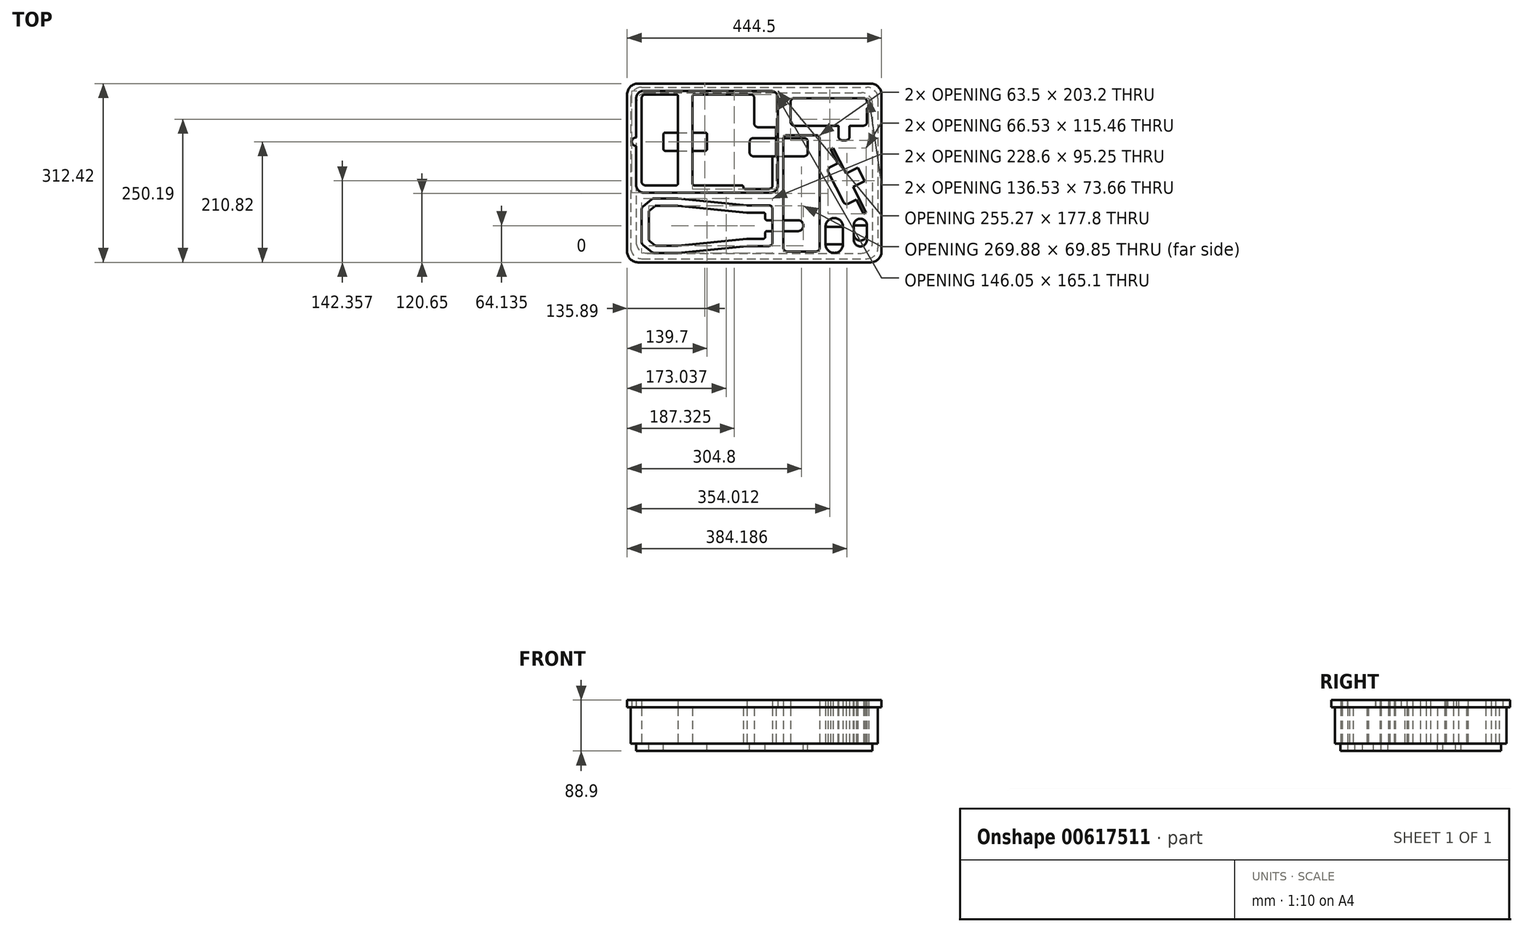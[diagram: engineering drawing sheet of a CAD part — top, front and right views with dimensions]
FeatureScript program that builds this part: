
annotation { "Feature Type Name" : "Feature", "Feature Type Description" : "" }
export const myFeature = defineFeature(function(context is Context, id is Id, definition is map)
    precondition{}
    {
        {
            var Q0;
            Q0=qCreatedBy(makeId("Top.planeOp"),FACE);
            var sketch = newSketch(context, id + "F0", { "sketchPlane" : qUnion([Q0])});
            skLineSegment(sketch, "E0.bottom", {"start": v(-196.85, 149.86) * mm, "end": v(196.85, 149.86) * mm});
            skLineSegment(sketch, "E0.top", {"start": v(-196.85, -149.86) * mm, "end": v(196.85, -149.86) * mm});
            skLineSegment(sketch, "E0.left", {"start": v(-215.9, 130.81) * mm, "end": v(-215.9, -130.81) * mm});
            skLineSegment(sketch, "E0.right", {"start": v(215.9, 130.81) * mm, "end": v(215.9, -130.8) * mm});
            skLineSegment(sketch, "E1.bottom", {"start": v(-196.85, -15.24) * mm, "end": v(-196.85, 130.81) * mm});
            skLineSegment(sketch, "E1.top", {"start": v(31.75, -21.59) * mm, "end": v(31.75, 26.04) * mm});
            skLineSegment(sketch, "E1.right", {"start": v(-190.5, 137.16) * mm, "end": v(-136.52, 137.16) * mm});
            skLineSegment(sketch, "E2.bottom", {"start": v(124.46, -93.98) * mm, "end": v(154.94, -93.98) * mm});
            skLineSegment(sketch, "E2.top", {"start": v(124.46, -124.46) * mm, "end": v(154.94, -124.46) * mm});
            skLineSegment(sketch, "E2.left", {"start": v(124.46, -93.98) * mm, "end": v(124.46, -124.46) * mm});
            skLineSegment(sketch, "E2.right", {"start": v(154.94, -93.98) * mm, "end": v(154.94, -124.46) * mm});
            skLineSegment(sketch, "E3", {"start": v(142.6, -24.8) * mm, "end": v(186.74, -2.32) * mm, "construction": true});
            skLineSegment(sketch, "E4", {"start": v(142.6, -24.8) * mm, "end": v(155.87, -50.83) * mm});
            skLineSegment(sketch, "E5", {"start": v(164.4, -53.6) * mm, "end": v(177.99, -46.7) * mm});
            skLineSegment(sketch, "E6", {"start": v(177.99, -46.7) * mm, "end": v(190.67, -71.59) * mm});
            skLineSegment(sketch, "E7", {"start": v(190.67, -71.59) * mm, "end": v(195.2, -69.28) * mm});
            skLineSegment(sketch, "E8", {"start": v(160.32, -0.82) * mm, "end": v(180.68, 9.56) * mm});
            skLineSegment(sketch, "E9", {"start": v(180.68, 9.56) * mm, "end": v(186.74, -2.32) * mm});
            skPoint(sketch, "E10.visualSharp", {"position": v(158.75, -56.5) * mm});
            skArc(sketch, "E10.filletArc", {"start": v(155.87, -50.83) * mm, "mid": v(159.56, -54) * mm, "end": v(164.4, -53.6) * mm});
            skArc(sketch, "E11.MirrorCS", {"start": v(129.35, 1.22) * mm, "mid": v(128.96, 6.06) * mm, "end": v(132.12, 9.76) * mm});
            skLineSegment(sketch, "E12.MirrorCS", {"start": v(145.7, 16.68) * mm, "end": v(133.02, 41.57) * mm});
            skLineSegment(sketch, "E13.MirrorCS", {"start": v(132.12, 9.76) * mm, "end": v(145.7, 16.68) * mm});
            skPoint(sketch, "E14.MirrorP", {"position": v(126.46, 6.88) * mm});
            skLineSegment(sketch, "E15.MirrorCS", {"start": v(172.42, -24.58) * mm, "end": v(192.8, -14.2) * mm});
            skLineSegment(sketch, "E16.MirrorCS", {"start": v(142.6, -24.8) * mm, "end": v(129.35, 1.22) * mm});
            skLineSegment(sketch, "E17.MirrorCS", {"start": v(192.8, -14.2) * mm, "end": v(186.74, -2.32) * mm});
            skLineSegment(sketch, "E18", {"start": v(172.42, -24.58) * mm, "end": v(195.2, -69.28) * mm});
            skPoint(sketch, "E19.visualSharp", {"position": v(-215.9, 149.86) * mm});
            skArc(sketch, "E19.filletArc", {"start": v(-196.85, 149.86) * mm, "mid": v(-210.32, 144.28) * mm, "end": v(-215.9, 130.81) * mm});
            skPoint(sketch, "E20.visualSharp", {"position": v(215.9, 149.86) * mm});
            skArc(sketch, "E20.filletArc", {"start": v(215.9, 130.81) * mm, "mid": v(210.32, 144.28) * mm, "end": v(196.85, 149.86) * mm});
            skPoint(sketch, "E21.visualSharp", {"position": v(215.9, -149.86) * mm});
            skArc(sketch, "E21.filletArc", {"start": v(196.85, -149.86) * mm, "mid": v(210.32, -144.28) * mm, "end": v(215.9, -130.8) * mm});
            skPoint(sketch, "E22.visualSharp", {"position": v(-215.9, -149.86) * mm});
            skArc(sketch, "E22.filletArc", {"start": v(-215.9, -130.81) * mm, "mid": v(-210.32, -144.28) * mm, "end": v(-196.85, -149.86) * mm});
            skPoint(sketch, "E23.visualSharp", {"position": v(-196.85, -27.94) * mm});
            skPoint(sketch, "E24.visualSharp", {"position": v(31.75, -27.94) * mm});
            skArc(sketch, "E24.filletArc", {"start": v(25.4, -27.94) * mm, "mid": v(29.9, -26.08) * mm, "end": v(31.75, -21.59) * mm});
            skPoint(sketch, "E25.visualSharp", {"position": v(-196.85, 137.16) * mm});
            skArc(sketch, "E25.filletArc", {"start": v(-190.5, 137.16) * mm, "mid": v(-195, 135.3) * mm, "end": v(-196.85, 130.81) * mm});
            skPoint(sketch, "E26.visualSharp", {"position": v(31.75, 137.16) * mm});
            skArc(sketch, "E26.filletArc", {"start": v(31.75, 130.81) * mm, "mid": v(29.9, 135.3) * mm, "end": v(25.4, 137.16) * mm, "construction": true});
            skLineSegment(sketch, "E27.bottom", {"start": v(63.5, 88.9) * mm, "end": v(63.5, 124.46) * mm});
            skLineSegment(sketch, "E27.top", {"start": v(196.85, 88.9) * mm, "end": v(196.85, 112.08) * mm});
            skLineSegment(sketch, "E27.left", {"start": v(69.85, 82.55) * mm, "end": v(146.05, 82.55) * mm});
            skLineSegment(sketch, "E27.right", {"start": v(69.85, 130.81) * mm, "end": v(190.5, 130.81) * mm});
            skLineSegment(sketch, "E28.bottom", {"start": v(147.32, 81.28) * mm, "end": v(147.32, 63.5) * mm});
            skLineSegment(sketch, "E28.top", {"start": v(166.37, 81.28) * mm, "end": v(166.37, 63.5) * mm});
            skLineSegment(sketch, "E28.right", {"start": v(153.67, 57.15) * mm, "end": v(160.02, 57.15) * mm});
            skLineSegment(sketch, "E29.trimOffspring", {"start": v(167.64, 82.55) * mm, "end": v(190.5, 82.55) * mm});
            skLineSegment(sketch, "E30", {"start": v(147.32, 82.55) * mm, "end": v(166.37, 82.55) * mm, "construction": true});
            skPoint(sketch, "E31.visualSharp", {"position": v(63.5, 82.55) * mm});
            skArc(sketch, "E31.filletArc", {"start": v(63.5, 88.9) * mm, "mid": v(65.36, 84.4) * mm, "end": v(69.85, 82.55) * mm});
            skPoint(sketch, "E32.visualSharp", {"position": v(196.85, 82.55) * mm});
            skArc(sketch, "E32.filletArc", {"start": v(190.5, 82.55) * mm, "mid": v(195, 84.4) * mm, "end": v(196.85, 88.9) * mm});
            skArc(sketch, "E33.filletArc", {"start": v(196.85, 124.46) * mm, "mid": v(195, 128.95) * mm, "end": v(190.5, 130.81) * mm});
            skPoint(sketch, "E34.visualSharp", {"position": v(63.5, 130.81) * mm});
            skArc(sketch, "E34.filletArc", {"start": v(69.85, 130.81) * mm, "mid": v(65.36, 128.95) * mm, "end": v(63.5, 124.46) * mm});
            skPoint(sketch, "E35.visualSharp", {"position": v(147.32, 57.15) * mm});
            skArc(sketch, "E35.filletArc", {"start": v(147.32, 63.5) * mm, "mid": v(149.18, 59) * mm, "end": v(153.67, 57.15) * mm});
            skPoint(sketch, "E36.visualSharp", {"position": v(166.37, 57.15) * mm});
            skArc(sketch, "E36.filletArc", {"start": v(160.02, 57.15) * mm, "mid": v(164.51, 59) * mm, "end": v(166.37, 63.5) * mm});
            skLineSegment(sketch, "E37.bottom", {"start": v(173.74, -91.44) * mm, "end": v(196.85, -91.44) * mm});
            skLineSegment(sketch, "E37.left", {"start": v(173.74, -91.44) * mm, "end": v(173.74, -106.68) * mm});
            skLineSegment(sketch, "E37.right", {"start": v(196.85, -91.44) * mm, "end": v(196.85, -106.68) * mm});
            skArc(sketch, "E38", {"start": v(173.74, -106.68) * mm, "mid": v(185.3, -118.24) * mm, "end": v(196.85, -106.68) * mm});
            skLineSegment(sketch, "E39.bottom", {"start": v(-196.85, -139.7) * mm, "end": v(-196.85, -44.45) * mm, "construction": true});
            skLineSegment(sketch, "E39.top", {"start": v(31.75, -139.7) * mm, "end": v(31.75, -44.45) * mm, "construction": true});
            skLineSegment(sketch, "E39.left", {"start": v(-196.85, -139.7) * mm, "end": v(31.75, -139.7) * mm, "construction": true});
            skLineSegment(sketch, "E39.right", {"start": v(-196.85, -44.45) * mm, "end": v(31.75, -44.45) * mm, "construction": true});
            skLineSegment(sketch, "E40", {"start": v(-196.85, -92.08) * mm, "end": v(31.75, -92.07) * mm, "construction": true});
            skLineSegment(sketch, "E41", {"start": v(-196.85, -123.83) * mm, "end": v(31.75, -123.82) * mm, "construction": true});
            skLineSegment(sketch, "E42.MirrorCS", {"start": v(-196.85, -60.33) * mm, "end": v(31.75, -60.32) * mm, "construction": true});
            skLineSegment(sketch, "E43", {"start": v(-196.85, -127.64) * mm, "end": v(31.75, -127.63) * mm, "construction": true});
            skLineSegment(sketch, "E44.MirrorCS", {"start": v(-196.85, -56.51) * mm, "end": v(31.75, -56.51) * mm, "construction": true});
            skLineSegment(sketch, "E45", {"start": v(-177.16, -139.7) * mm, "end": v(-177.16, -44.45) * mm, "construction": true});
            skLineSegment(sketch, "E46", {"start": v(-133.35, -139.7) * mm, "end": v(-133.35, -44.45) * mm, "construction": true});
            skLineSegment(sketch, "E47", {"start": v(-12.7, -139.7) * mm, "end": v(-12.7, -44.45) * mm, "construction": true});
            skLineSegment(sketch, "E48", {"start": v(-196.85, -120.79) * mm, "end": v(-196.85, -63.36) * mm});
            skLineSegment(sketch, "E49", {"start": v(-194.49, -58.42) * mm, "end": v(-178.9, -45.86) * mm});
            skLineSegment(sketch, "E50", {"start": v(-174.92, -44.45) * mm, "end": v(-133.35, -44.45) * mm});
            skLineSegment(sketch, "E51", {"start": v(-133.35, -44.45) * mm, "end": v(-12.7, -56.51) * mm});
            skLineSegment(sketch, "E52", {"start": v(-12.7, -56.51) * mm, "end": v(25.4, -56.51) * mm});
            skLineSegment(sketch, "E53", {"start": v(31.75, -62.86) * mm, "end": v(31.75, -121.28) * mm});
            skLineSegment(sketch, "E54", {"start": v(25.4, -127.63) * mm, "end": v(-12.7, -127.63) * mm});
            skLineSegment(sketch, "E55", {"start": v(-12.7, -127.64) * mm, "end": v(-133.35, -139.7) * mm});
            skLineSegment(sketch, "E56", {"start": v(-133.35, -139.7) * mm, "end": v(-174.92, -139.7) * mm});
            skLineSegment(sketch, "E57", {"start": v(-178.9, -138.3) * mm, "end": v(-194.49, -125.73) * mm});
            skPoint(sketch, "E58.visualSharp", {"position": v(31.75, -127.64) * mm});
            skArc(sketch, "E58.filletArc", {"start": v(25.4, -127.63) * mm, "mid": v(29.9, -125.78) * mm, "end": v(31.75, -121.28) * mm});
            skPoint(sketch, "E59.visualSharp", {"position": v(31.75, -56.51) * mm});
            skArc(sketch, "E59.filletArc", {"start": v(31.75, -62.86) * mm, "mid": v(29.9, -58.37) * mm, "end": v(25.4, -56.51) * mm});
            skPoint(sketch, "E60.visualSharp", {"position": v(-196.85, -123.83) * mm});
            skArc(sketch, "E60.filletArc", {"start": v(-196.85, -120.79) * mm, "mid": v(-196.23, -123.53) * mm, "end": v(-194.49, -125.73) * mm});
            skPoint(sketch, "E61.visualSharp", {"position": v(-177.16, -139.7) * mm});
            skArc(sketch, "E61.filletArc", {"start": v(-178.9, -138.3) * mm, "mid": v(-177.04, -139.34) * mm, "end": v(-174.92, -139.7) * mm});
            skPoint(sketch, "E62.visualSharp", {"position": v(-196.85, -60.33) * mm});
            skArc(sketch, "E62.filletArc", {"start": v(-194.49, -58.42) * mm, "mid": v(-196.23, -60.62) * mm, "end": v(-196.85, -63.36) * mm});
            skPoint(sketch, "E63.visualSharp", {"position": v(-177.16, -44.45) * mm});
            skArc(sketch, "E63.filletArc", {"start": v(-174.92, -44.45) * mm, "mid": v(-177.04, -44.81) * mm, "end": v(-178.9, -45.86) * mm});
            skLineSegment(sketch, "E64", {"start": v(173.74, -106.68) * mm, "end": v(196.85, -106.68) * mm, "construction": true});
            skLineSegment(sketch, "E65.MirrorCS", {"start": v(160.32, -0.82) * mm, "end": v(137.54, 43.88) * mm});
            skLineSegment(sketch, "E66.MirrorCS", {"start": v(133.02, 41.57) * mm, "end": v(137.54, 43.88) * mm});
            skLineSegment(sketch, "E67", {"start": v(198.12, 122.87) * mm, "end": v(198.76, 122.87) * mm});
            skLineSegment(sketch, "E68", {"start": v(200.02, 121.6) * mm, "end": v(200.02, 114.62) * mm});
            skLineSegment(sketch, "E69", {"start": v(198.76, 113.35) * mm, "end": v(198.12, 113.35) * mm});
            skPoint(sketch, "E70.visualSharp", {"position": v(166.37, 82.55) * mm});
            skArc(sketch, "E70.filletArc", {"start": v(167.64, 82.55) * mm, "mid": v(166.74, 82.18) * mm, "end": v(166.37, 81.28) * mm});
            skPoint(sketch, "E71.visualSharp", {"position": v(147.32, 82.55) * mm});
            skArc(sketch, "E71.filletArc", {"start": v(147.32, 81.28) * mm, "mid": v(146.95, 82.18) * mm, "end": v(146.05, 82.55) * mm});
            skPoint(sketch, "E72.visualSharp", {"position": v(200.03, 113.35) * mm});
            skArc(sketch, "E72.filletArc", {"start": v(198.76, 113.35) * mm, "mid": v(199.65, 113.72) * mm, "end": v(200.03, 114.62) * mm});
            skPoint(sketch, "E73.visualSharp", {"position": v(200.03, 122.87) * mm});
            skArc(sketch, "E73.filletArc", {"start": v(200.02, 121.6) * mm, "mid": v(199.65, 122.5) * mm, "end": v(198.76, 122.87) * mm});
            skPoint(sketch, "E74.visualSharp", {"position": v(196.85, 122.87) * mm});
            skArc(sketch, "E74.filletArc", {"start": v(196.85, 124.13) * mm, "mid": v(197.23, 123.24) * mm, "end": v(198.12, 122.87) * mm});
            skPoint(sketch, "E75.visualSharp", {"position": v(196.85, 113.35) * mm});
            skArc(sketch, "E75.filletArc", {"start": v(198.12, 113.35) * mm, "mid": v(197.22, 112.98) * mm, "end": v(196.85, 112.08) * mm});
            skLineSegment(sketch, "E76", {"start": v(-196.85, 54.61) * mm, "end": v(31.75, 54.61) * mm, "construction": true});
            skLineSegment(sketch, "E77", {"start": v(-82.55, -27.94) * mm, "end": v(-82.55, 137.16) * mm, "construction": true});
            skLineSegment(sketch, "E78", {"start": v(0, 149.86) * mm, "end": v(0, -149.86) * mm, "construction": true});
            skLineSegment(sketch, "E79", {"start": v(-215.9, 0) * mm, "end": v(215.9, 0) * mm, "construction": true});
            skPoint(sketch, "E80", {"position": v(0, 0) * mm});
            skPoint(sketch, "E81", {"position": v(-82.55, 54.61) * mm});
            skPoint(sketch, "E82", {"position": v(-133.35, -92.08) * mm});
            skLineSegment(sketch, "E83", {"start": v(63.5, 106.68) * mm, "end": v(196.85, 106.68) * mm, "construction": true});
            skLineSegment(sketch, "E84", {"start": v(130.18, 130.81) * mm, "end": v(130.18, 82.55) * mm, "construction": true});
            skPoint(sketch, "E85", {"position": v(130.18, 106.68) * mm});
            skLineSegment(sketch, "E86", {"start": v(172.42, -24.58) * mm, "end": v(160.32, -0.82) * mm, "construction": true});
            skPoint(sketch, "E87", {"position": v(166.37, -12.7) * mm});
            skLineSegment(sketch, "E88", {"start": v(196.85, 124.46) * mm, "end": v(196.85, 124.13) * mm});
            skLineSegment(sketch, "E89", {"start": v(196.85, 124.13) * mm, "end": v(196.85, 112.08) * mm, "construction": true});
            skArc(sketch, "E90", {"start": v(31.75, -21.59) * mm, "mid": v(29.9, -26.08) * mm, "end": v(25.4, -27.94) * mm});
            skLineSegment(sketch, "E91.bottom", {"start": v(107.95, -137.16) * mm, "end": v(57.15, -137.16) * mm});
            skLineSegment(sketch, "E91.top", {"start": v(107.95, 66.04) * mm, "end": v(57.15, 66.04) * mm});
            skLineSegment(sketch, "E91.left", {"start": v(114.3, -130.8) * mm, "end": v(114.3, 59.7) * mm});
            skLineSegment(sketch, "E91.right", {"start": v(50.8, -130.8) * mm, "end": v(50.8, 59.7) * mm});
            skLineSegment(sketch, "E92", {"start": v(82.55, -137.16) * mm, "end": v(82.55, 66.04) * mm, "construction": true});
            skLineSegment(sketch, "E93", {"start": v(114.3, -35.56) * mm, "end": v(50.8, -35.56) * mm, "construction": true});
            skPoint(sketch, "E94", {"position": v(82.55, -35.56) * mm});
            skPoint(sketch, "E95.visualSharp", {"position": v(114.3, -137.16) * mm});
            skArc(sketch, "E95.filletArc", {"start": v(107.95, -137.16) * mm, "mid": v(112.44, -135.3) * mm, "end": v(114.3, -130.8) * mm});
            skPoint(sketch, "E96.visualSharp", {"position": v(50.8, -137.16) * mm});
            skArc(sketch, "E96.filletArc", {"start": v(50.8, -130.8) * mm, "mid": v(52.66, -135.3) * mm, "end": v(57.15, -137.16) * mm});
            skPoint(sketch, "E97.visualSharp", {"position": v(50.8, 66.04) * mm});
            skArc(sketch, "E97.filletArc", {"start": v(57.15, 66.04) * mm, "mid": v(52.66, 64.18) * mm, "end": v(50.8, 59.7) * mm});
            skPoint(sketch, "E98.visualSharp", {"position": v(114.3, 66.04) * mm});
            skArc(sketch, "E98.filletArc", {"start": v(114.3, 59.7) * mm, "mid": v(112.44, 64.18) * mm, "end": v(107.95, 66.04) * mm});
            skLineSegment(sketch, "E99.left", {"start": v(-107.95, 133.99) * mm, "end": v(-107.95, -18.41) * mm});
            skLineSegment(sketch, "E99.right", {"start": v(-133.35, 133.99) * mm, "end": v(-133.35, -18.41) * mm});
            skLineSegment(sketch, "E100", {"start": v(34.93, 80.01) * mm, "end": v(34.92, 80.01) * mm});
            skLineSegment(sketch, "E101.MirrorCS", {"start": v(34.93, 29.21) * mm, "end": v(34.93, 29.21) * mm});
            skLineSegment(sketch, "E102", {"start": v(38.1, 76.84) * mm, "end": v(38.1, 32.39) * mm});
            skLineSegment(sketch, "E103", {"start": v(-104.77, 137.16) * mm, "end": v(-6.35, 137.16) * mm});
            skLineSegment(sketch, "E104", {"start": v(31.75, 83.19) * mm, "end": v(31.75, 130.81) * mm, "construction": true});
            skLineSegment(sketch, "E105", {"start": v(31.75, 29.21) * mm, "end": v(31.75, 80.01) * mm, "construction": true});
            skLineSegment(sketch, "E106", {"start": v(-133.35, 137.16) * mm, "end": v(-107.95, 137.16) * mm, "construction": true});
            skPoint(sketch, "E107.visualSharp", {"position": v(-107.95, 137.16) * mm});
            skArc(sketch, "E107.filletArc", {"start": v(-104.77, 137.16) * mm, "mid": v(-107.02, 136.23) * mm, "end": v(-107.95, 133.99) * mm});
            skPoint(sketch, "E108.visualSharp", {"position": v(-133.35, 137.16) * mm});
            skArc(sketch, "E108.filletArc", {"start": v(-133.35, 133.99) * mm, "mid": v(-134.28, 136.23) * mm, "end": v(-136.52, 137.16) * mm});
            skPoint(sketch, "E109.visualSharp", {"position": v(31.75, 80.01) * mm});
            skPoint(sketch, "E110.visualSharp", {"position": v(31.75, 29.21) * mm});
            skArc(sketch, "E110.filletArc", {"start": v(34.93, 29.21) * mm, "mid": v(32.68, 28.28) * mm, "end": v(31.75, 26.04) * mm});
            skPoint(sketch, "E111.visualSharp", {"position": v(38.1, 29.21) * mm});
            skArc(sketch, "E111.filletArc", {"start": v(34.93, 29.21) * mm, "mid": v(37.17, 30.14) * mm, "end": v(38.1, 32.39) * mm});
            skPoint(sketch, "E112.visualSharp", {"position": v(38.1, 80.01) * mm});
            skArc(sketch, "E112.filletArc", {"start": v(38.1, 76.84) * mm, "mid": v(37.17, 79.08) * mm, "end": v(34.92, 80.01) * mm});
            skLineSegment(sketch, "E113", {"start": v(0, 130.81) * mm, "end": v(0, 86.36) * mm});
            skLineSegment(sketch, "E114", {"start": v(6.35, 80.01) * mm, "end": v(34.93, 80.01) * mm});
            skPoint(sketch, "E115.visualSharp", {"position": v(0, 80.01) * mm});
            skArc(sketch, "E115.filletArc", {"start": v(0, 86.36) * mm, "mid": v(1.86, 81.87) * mm, "end": v(6.35, 80.01) * mm});
            skLineSegment(sketch, "E116", {"start": v(-6.35, 137.16) * mm, "end": v(0, 137.16) * mm, "construction": true});
            skLineSegment(sketch, "E117", {"start": v(0, 137.16) * mm, "end": v(25.4, 137.16) * mm, "construction": true});
            skPoint(sketch, "E118.visualSharp", {"position": v(0, 137.16) * mm});
            skArc(sketch, "E118.filletArc", {"start": v(0, 130.81) * mm, "mid": v(-1.86, 135.3) * mm, "end": v(-6.35, 137.16) * mm});
            skLineSegment(sketch, "E119", {"start": v(-6.35, 137.16) * mm, "end": v(-6.35, 137.16) * mm});
            skLineSegment(sketch, "E120", {"start": v(-19.05, -24.76) * mm, "end": v(-19.05, -24.76) * mm});
            skLineSegment(sketch, "E121", {"start": v(-22.22, -21.59) * mm, "end": v(-104.78, -21.59) * mm});
            skLineSegment(sketch, "E122", {"start": v(-133.35, -21.59) * mm, "end": v(-133.35, -24.76) * mm, "construction": true});
            skLineSegment(sketch, "E123", {"start": v(-15.88, -27.94) * mm, "end": v(25.4, -27.94) * mm});
            skLineSegment(sketch, "E124", {"start": v(-107.95, -21.59) * mm, "end": v(-107.95, -24.76) * mm, "construction": true});
            skPoint(sketch, "E125.visualSharp", {"position": v(-196.85, -21.59) * mm});
            skArc(sketch, "E125.filletArc", {"start": v(-196.85, -15.24) * mm, "mid": v(-195, -19.73) * mm, "end": v(-190.5, -21.59) * mm});
            skPoint(sketch, "E126.visualSharp", {"position": v(-19.05, -21.59) * mm});
            skArc(sketch, "E126.filletArc", {"start": v(-19.05, -24.76) * mm, "mid": v(-19.98, -22.52) * mm, "end": v(-22.22, -21.59) * mm});
            skPoint(sketch, "E127.visualSharp", {"position": v(-19.05, -27.94) * mm});
            skArc(sketch, "E127.filletArc", {"start": v(-19.05, -24.76) * mm, "mid": v(-18.12, -27.01) * mm, "end": v(-15.88, -27.94) * mm});
            skLineSegment(sketch, "E128", {"start": v(-136.53, -21.59) * mm, "end": v(-190.5, -21.59) * mm});
            skPoint(sketch, "E129.visualSharp", {"position": v(-133.35, -21.59) * mm});
            skArc(sketch, "E129.filletArc", {"start": v(-136.53, -21.59) * mm, "mid": v(-134.28, -20.66) * mm, "end": v(-133.35, -18.41) * mm});
            skPoint(sketch, "E130.visualSharp", {"position": v(-107.95, -21.59) * mm});
            skArc(sketch, "E130.filletArc", {"start": v(-107.95, -18.41) * mm, "mid": v(-107.02, -20.66) * mm, "end": v(-104.78, -21.59) * mm});
            skSolve(sketch);
        }
        {
            var Q0;
            Q0=qSketchRegion(id+"F0",true);
            extrude(context, id + "F1", {"entities" : qUnion([Q0]), "depth" : 63.5 * mm, "offsetDistance" : 25.4 * mm});
        }
        {
            var Q0;
            Q0=qCreatedBy(makeId("Top.planeOp"),FACE);
            var sketch = newSketch(context, id + "F2", { "sketchPlane" : qUnion([Q0])});
            skLineSegment(sketch, "E131.0", {"start": v(-215.9, 149.86) * mm, "end": v(215.9, 149.86) * mm, "construction": true});
            skLineSegment(sketch, "E132.0", {"start": v(-215.9, 149.86) * mm, "end": v(-215.9, -149.86) * mm, "construction": true});
            skLineSegment(sketch, "E133.0", {"start": v(215.9, 149.86) * mm, "end": v(215.9, -149.86) * mm, "construction": true});
            skLineSegment(sketch, "E134.0", {"start": v(-190.26, -149.86) * mm, "end": v(215.9, -149.86) * mm, "construction": true});
            skPoint(sketch, "E135.orphan", {"position": v(-196.85, 149.86) * mm});
            skPoint(sketch, "E136.orphan", {"position": v(-215.9, 130.81) * mm});
            skPoint(sketch, "E137.orphan", {"position": v(196.85, 149.86) * mm});
            skPoint(sketch, "E138.orphan", {"position": v(215.9, 130.81) * mm});
            skPoint(sketch, "E139.orphan", {"position": v(215.9, -130.8) * mm});
            skPoint(sketch, "E140.orphan", {"position": v(196.85, -149.86) * mm});
            skPoint(sketch, "E141.orphan", {"position": v(-196.85, -149.86) * mm});
            skPoint(sketch, "E142.orphan", {"position": v(-215.9, -130.81) * mm});
            skPoint(sketch, "E143", {"position": v(0, 0) * mm});
            skLineSegment(sketch, "E144", {"start": v(0, 149.86) * mm, "end": v(0, -149.86) * mm, "construction": true});
            skPoint(sketch, "E144.startSnap0", {"position": v(0, 149.86) * mm});
            skLineSegment(sketch, "E145", {"start": v(-215.9, 0) * mm, "end": v(215.9, 0) * mm, "construction": true});
            skLineSegment(sketch, "E146.bottom", {"start": v(-187.32, 140.34) * mm, "end": v(187.33, 140.34) * mm});
            skLineSegment(sketch, "E146.top", {"start": v(-187.33, -140.33) * mm, "end": v(187.32, -140.33) * mm});
            skLineSegment(sketch, "E146.left", {"start": v(-206.38, 121.29) * mm, "end": v(-206.38, -121.28) * mm});
            skLineSegment(sketch, "E146.right", {"start": v(206.38, 121.29) * mm, "end": v(206.38, -121.28) * mm});
            skPoint(sketch, "E147.visualSharp", {"position": v(-206.38, 140.34) * mm});
            skPoint(sketch, "E148.visualSharp", {"position": v(206.38, 140.34) * mm});
            skPoint(sketch, "E149.visualSharp", {"position": v(206.38, -140.33) * mm});
            skPoint(sketch, "E150.visualSharp", {"position": v(-206.38, -140.33) * mm});
            skLineSegment(sketch, "E151.0.0", {"start": v(-12.7, -127.63) * mm, "end": v(25.4, -127.63) * mm, "construction": true});
            skArc(sketch, "E151.0.1", {"start": v(25.4, -127.63) * mm, "mid": v(29.9, -125.78) * mm, "end": v(31.75, -121.28) * mm, "construction": true});
            skLineSegment(sketch, "E151.0.2", {"start": v(31.75, -121.28) * mm, "end": v(31.75, -62.86) * mm, "construction": true});
            skArc(sketch, "E151.0.3", {"start": v(31.75, -62.86) * mm, "mid": v(29.9, -58.37) * mm, "end": v(25.4, -56.51) * mm, "construction": true});
            skLineSegment(sketch, "E151.0.4", {"start": v(25.4, -56.51) * mm, "end": v(-12.7, -56.51) * mm, "construction": true});
            skLineSegment(sketch, "E151.0.5", {"start": v(-12.7, -56.52) * mm, "end": v(-133.35, -44.45) * mm, "construction": true});
            skLineSegment(sketch, "E151.0.6", {"start": v(-133.35, -44.45) * mm, "end": v(-174.92, -44.45) * mm, "construction": true});
            skArc(sketch, "E151.0.7", {"start": v(-174.92, -44.45) * mm, "mid": v(-177.04, -44.81) * mm, "end": v(-178.9, -45.86) * mm, "construction": true});
            skLineSegment(sketch, "E151.0.8", {"start": v(-178.9, -45.86) * mm, "end": v(-194.49, -58.42) * mm, "construction": true});
            skArc(sketch, "E151.0.9", {"start": v(-194.49, -58.42) * mm, "mid": v(-196.23, -60.62) * mm, "end": v(-196.85, -63.36) * mm, "construction": true});
            skLineSegment(sketch, "E151.0.10", {"start": v(-196.85, -63.36) * mm, "end": v(-196.85, -120.79) * mm, "construction": true});
            skArc(sketch, "E151.0.11", {"start": v(-196.85, -120.79) * mm, "mid": v(-196.23, -123.53) * mm, "end": v(-194.49, -125.73) * mm, "construction": true});
            skLineSegment(sketch, "E151.0.12", {"start": v(-194.49, -125.73) * mm, "end": v(-178.9, -138.3) * mm, "construction": true});
            skArc(sketch, "E151.0.13", {"start": v(-178.9, -138.3) * mm, "mid": v(-177.04, -139.34) * mm, "end": v(-174.92, -139.7) * mm, "construction": true});
            skLineSegment(sketch, "E151.0.14", {"start": v(-174.92, -139.7) * mm, "end": v(-133.35, -139.7) * mm, "construction": true});
            skLineSegment(sketch, "E151.0.15", {"start": v(-133.35, -139.7) * mm, "end": v(-12.7, -127.64) * mm, "construction": true});
            skArc(sketch, "E152.filletArc", {"start": v(-187.32, 140.34) * mm, "mid": v(-200.8, 134.76) * mm, "end": v(-206.38, 121.29) * mm});
            skArc(sketch, "E153.filletArc", {"start": v(206.38, 121.29) * mm, "mid": v(200.8, 134.76) * mm, "end": v(187.33, 140.34) * mm});
            skArc(sketch, "E154.filletArc", {"start": v(187.32, -140.33) * mm, "mid": v(200.8, -134.76) * mm, "end": v(206.37, -121.28) * mm});
            skArc(sketch, "E155.filletArc", {"start": v(-206.38, -121.28) * mm, "mid": v(-200.8, -134.76) * mm, "end": v(-187.33, -140.33) * mm});
            skLineSegment(sketch, "E156.0", {"start": v(-173.55, -57.85) * mm, "end": v(-182.97, -65.45) * mm});
            skLineSegment(sketch, "E156.1", {"start": v(-134.14, -57.15) * mm, "end": v(-171.56, -57.15) * mm});
            skLineSegment(sketch, "E156.2", {"start": v(-184.15, -67.92) * mm, "end": v(-184.15, -116.23) * mm});
            skLineSegment(sketch, "E156.3", {"start": v(-13.5, -69.2) * mm, "end": v(-133.83, -57.17) * mm});
            skLineSegment(sketch, "E156.4", {"start": v(15.88, -69.21) * mm, "end": v(-13.18, -69.21) * mm});
            skLineSegment(sketch, "E156.5", {"start": v(19.05, -111.76) * mm, "end": v(19.05, -104.78) * mm});
            skLineSegment(sketch, "E156.6", {"start": v(-182.97, -118.7) * mm, "end": v(-173.55, -126.3) * mm});
            skLineSegment(sketch, "E156.7", {"start": v(-171.56, -127) * mm, "end": v(-134.14, -127) * mm});
            skLineSegment(sketch, "E156.8", {"start": v(-133.83, -126.98) * mm, "end": v(-13.5, -114.95) * mm});
            skLineSegment(sketch, "E156.9", {"start": v(-13.18, -114.93) * mm, "end": v(15.88, -114.93) * mm});
            skLineSegment(sketch, "E157", {"start": v(22.23, -82.55) * mm, "end": v(76.2, -82.55) * mm});
            skLineSegment(sketch, "E158", {"start": v(-184.15, -92.08) * mm, "end": v(76.2, -92.08) * mm, "construction": true});
            skLineSegment(sketch, "E159", {"start": v(76.2, -82.55) * mm, "end": v(76.2, -92.08) * mm, "construction": true});
            skLineSegment(sketch, "E160.MirrorCS", {"start": v(22.23, -101.6) * mm, "end": v(76.2, -101.6) * mm});
            skLineSegment(sketch, "E161.MirrorCS", {"start": v(76.2, -101.6) * mm, "end": v(76.2, -92.08) * mm, "construction": true});
            skLineSegment(sketch, "E162", {"start": v(19.05, -79.37) * mm, "end": v(19.05, -72.39) * mm});
            skPoint(sketch, "E163.orphan", {"position": v(19.05, -92.08) * mm});
            skArc(sketch, "E164", {"start": v(76.2, -82.55) * mm, "mid": v(85.73, -92.08) * mm, "end": v(76.2, -101.6) * mm});
            skLineSegment(sketch, "E165.bottom", {"start": v(-1.78, 60.96) * mm, "end": v(87.12, 60.96) * mm});
            skLineSegment(sketch, "E165.top", {"start": v(-1.78, 29.21) * mm, "end": v(87.12, 29.21) * mm});
            skLineSegment(sketch, "E165.left", {"start": v(-8.13, 54.61) * mm, "end": v(-8.13, 35.56) * mm});
            skLineSegment(sketch, "E165.right", {"start": v(93.47, 54.61) * mm, "end": v(93.47, 35.56) * mm});
            skPoint(sketch, "E166.visualSharp", {"position": v(-8.13, 60.96) * mm});
            skArc(sketch, "E166.filletArc", {"start": v(-1.78, 60.96) * mm, "mid": v(-6.27, 59.1) * mm, "end": v(-8.13, 54.61) * mm});
            skPoint(sketch, "E167.visualSharp", {"position": v(93.47, 60.96) * mm});
            skArc(sketch, "E167.filletArc", {"start": v(93.47, 54.61) * mm, "mid": v(91.61, 59.1) * mm, "end": v(87.12, 60.96) * mm});
            skPoint(sketch, "E168.visualSharp", {"position": v(93.47, 29.21) * mm});
            skArc(sketch, "E168.filletArc", {"start": v(87.12, 29.21) * mm, "mid": v(91.61, 31.07) * mm, "end": v(93.47, 35.56) * mm});
            skPoint(sketch, "E169.visualSharp", {"position": v(-8.13, 29.21) * mm});
            skArc(sketch, "E169.filletArc", {"start": v(-8.13, 35.56) * mm, "mid": v(-6.27, 31.07) * mm, "end": v(-1.78, 29.21) * mm});
            skPoint(sketch, "E170.visualSharp", {"position": v(19.05, -69.21) * mm});
            skArc(sketch, "E170.filletArc", {"start": v(19.05, -72.39) * mm, "mid": v(18.12, -70.14) * mm, "end": v(15.88, -69.21) * mm});
            skPoint(sketch, "E171.visualSharp", {"position": v(19.05, -82.55) * mm});
            skArc(sketch, "E171.filletArc", {"start": v(19.05, -79.37) * mm, "mid": v(19.98, -81.62) * mm, "end": v(22.23, -82.55) * mm});
            skPoint(sketch, "E172.visualSharp", {"position": v(19.05, -101.6) * mm});
            skArc(sketch, "E172.filletArc", {"start": v(22.23, -101.6) * mm, "mid": v(19.98, -102.53) * mm, "end": v(19.05, -104.78) * mm});
            skPoint(sketch, "E173.visualSharp", {"position": v(19.05, -114.94) * mm});
            skArc(sketch, "E173.filletArc", {"start": v(15.88, -114.94) * mm, "mid": v(18.12, -114) * mm, "end": v(19.05, -111.76) * mm});
            skPoint(sketch, "E174.visualSharp", {"position": v(-184.15, -66.4) * mm});
            skArc(sketch, "E174.filletArc", {"start": v(-182.97, -65.45) * mm, "mid": v(-183.84, -66.55) * mm, "end": v(-184.15, -67.92) * mm});
            skPoint(sketch, "E175.visualSharp", {"position": v(-172.68, -57.15) * mm});
            skArc(sketch, "E175.filletArc", {"start": v(-171.56, -57.15) * mm, "mid": v(-172.62, -57.33) * mm, "end": v(-173.55, -57.85) * mm});
            skPoint(sketch, "E176.visualSharp", {"position": v(-133.98, -57.15) * mm});
            skArc(sketch, "E176.filletArc", {"start": v(-133.83, -57.17) * mm, "mid": v(-133.98, -57.15) * mm, "end": v(-134.14, -57.15) * mm});
            skPoint(sketch, "E177.visualSharp", {"position": v(-184.15, -117.75) * mm});
            skArc(sketch, "E177.filletArc", {"start": v(-184.15, -116.23) * mm, "mid": v(-183.84, -117.6) * mm, "end": v(-182.97, -118.7) * mm});
            skPoint(sketch, "E178.visualSharp", {"position": v(-172.68, -127) * mm});
            skArc(sketch, "E178.filletArc", {"start": v(-173.55, -126.3) * mm, "mid": v(-172.62, -126.82) * mm, "end": v(-171.56, -127) * mm});
            skPoint(sketch, "E179.visualSharp", {"position": v(-133.98, -127) * mm});
            skArc(sketch, "E179.filletArc", {"start": v(-134.14, -127) * mm, "mid": v(-133.98, -127) * mm, "end": v(-133.83, -126.98) * mm});
            skPoint(sketch, "E180.visualSharp", {"position": v(-13.33, -114.93) * mm});
            skArc(sketch, "E180.filletArc", {"start": v(-13.18, -114.93) * mm, "mid": v(-13.33, -114.94) * mm, "end": v(-13.5, -114.95) * mm});
            skPoint(sketch, "E181.visualSharp", {"position": v(-13.33, -69.21) * mm});
            skArc(sketch, "E181.filletArc", {"start": v(-13.5, -69.2) * mm, "mid": v(-13.33, -69.21) * mm, "end": v(-13.18, -69.21) * mm});
            skLineSegment(sketch, "E182.0", {"start": v(-196.85, 54.61) * mm, "end": v(31.75, 54.61) * mm, "construction": true});
            skLineSegment(sketch, "E183.0", {"start": v(-133.35, 133.99) * mm, "end": v(-133.35, -18.41) * mm, "construction": true});
            skLineSegment(sketch, "E184.0", {"start": v(-107.95, 133.99) * mm, "end": v(-107.95, -18.41) * mm, "construction": true});
            skLineSegment(sketch, "E185", {"start": v(-158.75, 54.61) * mm, "end": v(-158.75, 67.31) * mm});
            skLineSegment(sketch, "E186", {"start": v(-155.57, 70.49) * mm, "end": v(-85.72, 70.49) * mm});
            skLineSegment(sketch, "E187", {"start": v(-82.55, 67.31) * mm, "end": v(-82.55, 54.61) * mm});
            skLineSegment(sketch, "E188.MirrorCS", {"start": v(-82.55, 41.91) * mm, "end": v(-82.55, 54.61) * mm});
            skLineSegment(sketch, "E189.MirrorCS", {"start": v(-158.75, 54.61) * mm, "end": v(-158.75, 41.91) * mm});
            skLineSegment(sketch, "E190.MirrorCS", {"start": v(-155.57, 38.74) * mm, "end": v(-85.72, 38.74) * mm});
            skPoint(sketch, "E191.visualSharp", {"position": v(-158.75, 70.49) * mm});
            skArc(sketch, "E191.filletArc", {"start": v(-155.57, 70.49) * mm, "mid": v(-157.82, 69.56) * mm, "end": v(-158.75, 67.31) * mm});
            skPoint(sketch, "E192.visualSharp", {"position": v(-158.75, 38.74) * mm});
            skArc(sketch, "E192.filletArc", {"start": v(-158.75, 41.91) * mm, "mid": v(-157.82, 39.66) * mm, "end": v(-155.57, 38.74) * mm});
            skPoint(sketch, "E193.visualSharp", {"position": v(-82.55, 38.74) * mm});
            skArc(sketch, "E193.filletArc", {"start": v(-85.72, 38.74) * mm, "mid": v(-83.48, 39.66) * mm, "end": v(-82.55, 41.91) * mm});
            skPoint(sketch, "E194.visualSharp", {"position": v(-82.55, 70.49) * mm});
            skArc(sketch, "E194.filletArc", {"start": v(-82.55, 67.31) * mm, "mid": v(-83.48, 69.56) * mm, "end": v(-85.72, 70.49) * mm});
            skSolve(sketch);
        }
        {
            var Q0;
            Q0=qSketchRegion(id+"F2",true);
            extrude(context, id + "F3", {"entities" : qUnion([Q0]), "oppositeDirection" : true, "depth" : 12.7 * mm, "offsetDistance" : 25.4 * mm});
        }
        {
            var Q0;
            Q0=makeQuery(id+"F1.opExtrude","CAP_FACE",FACE,{"disambiguationData":[OSD([sQuery(id+"F0.wireOp",EDGE,"E0.bottom"),sQuery(id+"F0.wireOp",EDGE,"E0.top"),sQuery(id+"F0.wireOp",EDGE,"E0.left"),sQuery(id+"F0.wireOp",EDGE,"E0.right"),sQuery(id+"F0.wireOp",EDGE,"E1.bottom"),sQuery(id+"F0.wireOp",EDGE,"E1.top"),sQuery(id+"F0.wireOp",EDGE,"E1.left"),sQuery(id+"F0.wireOp",EDGE,"E1.right"),sQuery(id+"F0.wireOp",EDGE,"E2.bottom"),sQuery(id+"F0.wireOp",EDGE,"E2.top"),sQuery(id+"F0.wireOp",EDGE,"E2.left"),sQuery(id+"F0.wireOp",EDGE,"E2.right"),sQuery(id+"F0.wireOp",EDGE,"E4"),sQuery(id+"F0.wireOp",EDGE,"E5"),sQuery(id+"F0.wireOp",EDGE,"E6"),sQuery(id+"F0.wireOp",EDGE,"E7"),sQuery(id+"F0.wireOp",EDGE,"E8"),sQuery(id+"F0.wireOp",EDGE,"E9"),sQuery(id+"F0.wireOp",EDGE,"E10.filletArc"),sQuery(id+"F0.wireOp",EDGE,"E11.MirrorCS"),sQuery(id+"F0.wireOp",EDGE,"E12.MirrorCS"),sQuery(id+"F0.wireOp",EDGE,"E13.MirrorCS"),sQuery(id+"F0.wireOp",EDGE,"E15.MirrorCS"),sQuery(id+"F0.wireOp",EDGE,"E16.MirrorCS"),sQuery(id+"F0.wireOp",EDGE,"E17.MirrorCS"),sQuery(id+"F0.wireOp",EDGE,"E18"),sQuery(id+"F0.wireOp",EDGE,"E19.filletArc"),sQuery(id+"F0.wireOp",EDGE,"E20.filletArc"),sQuery(id+"F0.wireOp",EDGE,"E21.filletArc"),sQuery(id+"F0.wireOp",EDGE,"E22.filletArc"),sQuery(id+"F0.wireOp",EDGE,"E23.filletArc"),sQuery(id+"F0.wireOp",EDGE,"E25.filletArc"),sQuery(id+"F0.wireOp",EDGE,"E26.filletArc"),sQuery(id+"F0.wireOp",EDGE,"E27.bottom"),sQuery(id+"F0.wireOp",EDGE,"E27.top"),sQuery(id+"F0.wireOp",EDGE,"E27.left"),sQuery(id+"F0.wireOp",EDGE,"E27.right"),sQuery(id+"F0.wireOp",EDGE,"E28.bottom"),sQuery(id+"F0.wireOp",EDGE,"E28.top"),sQuery(id+"F0.wireOp",EDGE,"E28.right"),sQuery(id+"F0.wireOp",EDGE,"E29.trimOffspring"),sQuery(id+"F0.wireOp",EDGE,"E31.filletArc"),sQuery(id+"F0.wireOp",EDGE,"E32.filletArc"),sQuery(id+"F0.wireOp",EDGE,"E33.filletArc"),sQuery(id+"F0.wireOp",EDGE,"E34.filletArc"),sQuery(id+"F0.wireOp",EDGE,"E35.filletArc"),sQuery(id+"F0.wireOp",EDGE,"E36.filletArc"),sQuery(id+"F0.wireOp",EDGE,"E37.bottom"),sQuery(id+"F0.wireOp",EDGE,"E37.left"),sQuery(id+"F0.wireOp",EDGE,"E37.right"),sQuery(id+"F0.wireOp",EDGE,"E38"),sQuery(id+"F0.wireOp",EDGE,"E48"),sQuery(id+"F0.wireOp",EDGE,"E49"),sQuery(id+"F0.wireOp",EDGE,"E50"),sQuery(id+"F0.wireOp",EDGE,"E51"),sQuery(id+"F0.wireOp",EDGE,"E52"),sQuery(id+"F0.wireOp",EDGE,"E53"),sQuery(id+"F0.wireOp",EDGE,"E54"),sQuery(id+"F0.wireOp",EDGE,"E55"),sQuery(id+"F0.wireOp",EDGE,"E56"),sQuery(id+"F0.wireOp",EDGE,"E57"),sQuery(id+"F0.wireOp",EDGE,"E58.filletArc"),sQuery(id+"F0.wireOp",EDGE,"E59.filletArc"),sQuery(id+"F0.wireOp",EDGE,"E60.filletArc"),sQuery(id+"F0.wireOp",EDGE,"E61.filletArc"),sQuery(id+"F0.wireOp",EDGE,"E62.filletArc"),sQuery(id+"F0.wireOp",EDGE,"E63.filletArc"),sQuery(id+"F0.wireOp",EDGE,"E65.MirrorCS"),sQuery(id+"F0.wireOp",EDGE,"E66.MirrorCS"),sQuery(id+"F0.wireOp",EDGE,"E67"),sQuery(id+"F0.wireOp",EDGE,"E68"),sQuery(id+"F0.wireOp",EDGE,"E69"),sQuery(id+"F0.wireOp",EDGE,"E70.filletArc"),sQuery(id+"F0.wireOp",EDGE,"E71.filletArc"),sQuery(id+"F0.wireOp",EDGE,"E72.filletArc"),sQuery(id+"F0.wireOp",EDGE,"E73.filletArc"),sQuery(id+"F0.wireOp",EDGE,"E74.filletArc"),sQuery(id+"F0.wireOp",EDGE,"E75.filletArc"),sQuery(id+"F0.wireOp",EDGE,"E88"),sQuery(id+"F0.wireOp",EDGE,"E90"),sQuery(id+"F0.wireOp",EDGE,"E91.bottom"),sQuery(id+"F0.wireOp",EDGE,"E91.top"),sQuery(id+"F0.wireOp",EDGE,"E91.left"),sQuery(id+"F0.wireOp",EDGE,"E91.right"),sQuery(id+"F0.wireOp",EDGE,"E95.filletArc"),sQuery(id+"F0.wireOp",EDGE,"E96.filletArc"),sQuery(id+"F0.wireOp",EDGE,"E97.filletArc"),sQuery(id+"F0.wireOp",EDGE,"E98.filletArc")])],"isStart":false});
            var sketch = newSketch(context, id + "F4", { "sketchPlane" : qUnion([Q0])});
            skLineSegment(sketch, "E195.bottom", {"start": v(-203.2, 156.21) * mm, "end": v(203.2, 156.21) * mm});
            skLineSegment(sketch, "E195.top", {"start": v(-203.2, -156.2) * mm, "end": v(203.2, -156.2) * mm});
            skLineSegment(sketch, "E195.left", {"start": v(-222.25, 137.16) * mm, "end": v(-222.25, -137.16) * mm});
            skLineSegment(sketch, "E195.right", {"start": v(222.25, 137.16) * mm, "end": v(222.25, -137.16) * mm});
            skLineSegment(sketch, "E196.bottom", {"start": v(-196.85, -21.59) * mm, "end": v(-196.85, 130.81) * mm, "construction": true});
            skLineSegment(sketch, "E196.top", {"start": v(31.75, -21.59) * mm, "end": v(31.75, 130.81) * mm, "construction": true});
            skLineSegment(sketch, "E196.left", {"start": v(-190.5, -27.94) * mm, "end": v(25.4, -27.94) * mm, "construction": true});
            skLineSegment(sketch, "E196.right", {"start": v(-190.5, 137.16) * mm, "end": v(25.4, 137.16) * mm, "construction": true});
            skLineSegment(sketch, "E197.bottom", {"start": v(124.46, -93.98) * mm, "end": v(154.94, -93.98) * mm});
            skLineSegment(sketch, "E197.top", {"start": v(124.46, -124.46) * mm, "end": v(154.94, -124.46) * mm});
            skLineSegment(sketch, "E197.left", {"start": v(124.46, -93.98) * mm, "end": v(124.46, -124.46) * mm});
            skLineSegment(sketch, "E197.right", {"start": v(154.94, -93.98) * mm, "end": v(154.94, -124.46) * mm});
            skLineSegment(sketch, "E198", {"start": v(142.6, -24.8) * mm, "end": v(186.74, -2.32) * mm, "construction": true});
            skLineSegment(sketch, "E199", {"start": v(142.6, -24.8) * mm, "end": v(155.87, -50.83) * mm});
            skLineSegment(sketch, "E200", {"start": v(164.4, -53.6) * mm, "end": v(177.99, -46.7) * mm});
            skLineSegment(sketch, "E201", {"start": v(177.99, -46.7) * mm, "end": v(190.67, -71.59) * mm});
            skLineSegment(sketch, "E202", {"start": v(190.67, -71.59) * mm, "end": v(195.2, -69.28) * mm});
            skLineSegment(sketch, "E203", {"start": v(160.32, -0.82) * mm, "end": v(180.68, 9.56) * mm});
            skLineSegment(sketch, "E204", {"start": v(180.68, 9.56) * mm, "end": v(186.74, -2.32) * mm});
            skPoint(sketch, "E205.visualSharp", {"position": v(158.75, -56.5) * mm});
            skArc(sketch, "E205.filletArc", {"start": v(155.87, -50.83) * mm, "mid": v(159.56, -54) * mm, "end": v(164.4, -53.6) * mm});
            skArc(sketch, "E206.MirrorCS", {"start": v(129.35, 1.22) * mm, "mid": v(128.96, 6.06) * mm, "end": v(132.12, 9.76) * mm});
            skLineSegment(sketch, "E207.MirrorCS", {"start": v(145.7, 16.68) * mm, "end": v(133.02, 41.57) * mm});
            skLineSegment(sketch, "E208.MirrorCS", {"start": v(132.12, 9.76) * mm, "end": v(145.7, 16.68) * mm});
            skPoint(sketch, "E209.MirrorP", {"position": v(126.46, 6.88) * mm});
            skLineSegment(sketch, "E210.MirrorCS", {"start": v(172.42, -24.58) * mm, "end": v(192.8, -14.2) * mm});
            skLineSegment(sketch, "E211.MirrorCS", {"start": v(142.6, -24.8) * mm, "end": v(129.35, 1.22) * mm});
            skLineSegment(sketch, "E212.MirrorCS", {"start": v(192.8, -14.2) * mm, "end": v(186.74, -2.32) * mm});
            skLineSegment(sketch, "E213", {"start": v(172.42, -24.58) * mm, "end": v(195.2, -69.28) * mm});
            skPoint(sketch, "E214.visualSharp", {"position": v(-222.25, 156.21) * mm});
            skArc(sketch, "E214.filletArc", {"start": v(-203.2, 156.21) * mm, "mid": v(-216.67, 150.63) * mm, "end": v(-222.25, 137.16) * mm});
            skPoint(sketch, "E215.visualSharp", {"position": v(222.25, 156.21) * mm});
            skArc(sketch, "E215.filletArc", {"start": v(222.25, 137.16) * mm, "mid": v(216.67, 150.63) * mm, "end": v(203.2, 156.21) * mm});
            skPoint(sketch, "E216.visualSharp", {"position": v(222.25, -156.2) * mm});
            skArc(sketch, "E216.filletArc", {"start": v(203.2, -156.2) * mm, "mid": v(216.67, -150.63) * mm, "end": v(222.25, -137.16) * mm});
            skPoint(sketch, "E217.visualSharp", {"position": v(-222.25, -156.2) * mm});
            skArc(sketch, "E217.filletArc", {"start": v(-222.25, -137.16) * mm, "mid": v(-216.67, -150.63) * mm, "end": v(-203.2, -156.21) * mm});
            skPoint(sketch, "E218.visualSharp", {"position": v(-196.85, -27.94) * mm});
            skArc(sketch, "E218.filletArc", {"start": v(-196.85, -21.59) * mm, "mid": v(-195, -26.08) * mm, "end": v(-190.5, -27.94) * mm, "construction": true});
            skPoint(sketch, "E219.visualSharp", {"position": v(31.75, -27.94) * mm});
            skArc(sketch, "E219.filletArc", {"start": v(25.4, -27.94) * mm, "mid": v(29.9, -26.08) * mm, "end": v(31.75, -21.59) * mm, "construction": true});
            skPoint(sketch, "E220.visualSharp", {"position": v(-196.85, 137.16) * mm});
            skArc(sketch, "E220.filletArc", {"start": v(-190.5, 137.16) * mm, "mid": v(-195, 135.3) * mm, "end": v(-196.85, 130.81) * mm, "construction": true});
            skPoint(sketch, "E221.visualSharp", {"position": v(31.75, 137.16) * mm});
            skArc(sketch, "E221.filletArc", {"start": v(31.75, 130.81) * mm, "mid": v(29.9, 135.3) * mm, "end": v(25.4, 137.16) * mm, "construction": true});
            skLineSegment(sketch, "E222.bottom", {"start": v(63.5, 88.9) * mm, "end": v(63.5, 124.46) * mm});
            skLineSegment(sketch, "E222.top", {"start": v(196.85, 88.9) * mm, "end": v(196.85, 112.08) * mm});
            skLineSegment(sketch, "E222.left", {"start": v(69.85, 82.55) * mm, "end": v(146.05, 82.55) * mm});
            skLineSegment(sketch, "E222.right", {"start": v(69.85, 130.81) * mm, "end": v(190.5, 130.81) * mm});
            skLineSegment(sketch, "E223.bottom", {"start": v(147.32, 81.28) * mm, "end": v(147.32, 63.5) * mm});
            skLineSegment(sketch, "E223.top", {"start": v(166.37, 81.28) * mm, "end": v(166.37, 63.5) * mm});
            skLineSegment(sketch, "E223.right", {"start": v(153.67, 57.15) * mm, "end": v(160.02, 57.15) * mm});
            skLineSegment(sketch, "E224.trimOffspring", {"start": v(167.64, 82.55) * mm, "end": v(190.5, 82.55) * mm});
            skLineSegment(sketch, "E225", {"start": v(147.32, 82.55) * mm, "end": v(166.37, 82.55) * mm, "construction": true});
            skPoint(sketch, "E226.visualSharp", {"position": v(63.5, 82.55) * mm});
            skArc(sketch, "E226.filletArc", {"start": v(63.5, 88.9) * mm, "mid": v(65.36, 84.4) * mm, "end": v(69.85, 82.55) * mm});
            skPoint(sketch, "E227.visualSharp", {"position": v(196.85, 82.55) * mm});
            skArc(sketch, "E227.filletArc", {"start": v(190.5, 82.55) * mm, "mid": v(195, 84.4) * mm, "end": v(196.85, 88.9) * mm});
            skPoint(sketch, "E228.visualSharp", {"position": v(196.85, 130.81) * mm});
            skArc(sketch, "E228.filletArc", {"start": v(196.85, 124.46) * mm, "mid": v(195, 128.95) * mm, "end": v(190.5, 130.81) * mm});
            skPoint(sketch, "E229.visualSharp", {"position": v(63.5, 130.81) * mm});
            skArc(sketch, "E229.filletArc", {"start": v(69.85, 130.81) * mm, "mid": v(65.36, 128.95) * mm, "end": v(63.5, 124.46) * mm});
            skPoint(sketch, "E230.visualSharp", {"position": v(147.32, 57.15) * mm});
            skArc(sketch, "E230.filletArc", {"start": v(147.32, 63.5) * mm, "mid": v(149.18, 59) * mm, "end": v(153.67, 57.15) * mm});
            skPoint(sketch, "E231.visualSharp", {"position": v(166.37, 57.15) * mm});
            skArc(sketch, "E231.filletArc", {"start": v(160.02, 57.15) * mm, "mid": v(164.51, 59) * mm, "end": v(166.37, 63.5) * mm});
            skLineSegment(sketch, "E232.bottom", {"start": v(173.74, -91.44) * mm, "end": v(196.85, -91.44) * mm, "construction": true});
            skLineSegment(sketch, "E232.left", {"start": v(173.74, -91.44) * mm, "end": v(173.74, -116.84) * mm});
            skLineSegment(sketch, "E232.right", {"start": v(196.85, -91.44) * mm, "end": v(196.85, -116.84) * mm});
            skArc(sketch, "E233", {"start": v(173.74, -116.84) * mm, "mid": v(185.3, -128.4) * mm, "end": v(196.85, -116.84) * mm});
            skLineSegment(sketch, "E234.bottom", {"start": v(-196.85, -139.7) * mm, "end": v(-196.85, -44.45) * mm, "construction": true});
            skLineSegment(sketch, "E234.top", {"start": v(31.75, -139.7) * mm, "end": v(31.75, -44.45) * mm, "construction": true});
            skLineSegment(sketch, "E234.left", {"start": v(-196.85, -139.7) * mm, "end": v(31.75, -139.7) * mm, "construction": true});
            skLineSegment(sketch, "E234.right", {"start": v(-196.85, -44.45) * mm, "end": v(31.75, -44.45) * mm, "construction": true});
            skLineSegment(sketch, "E235", {"start": v(-196.85, -92.07) * mm, "end": v(31.75, -92.07) * mm, "construction": true});
            skLineSegment(sketch, "E236", {"start": v(-196.85, -123.82) * mm, "end": v(31.75, -123.82) * mm, "construction": true});
            skLineSegment(sketch, "E237.MirrorCS", {"start": v(-196.85, -60.32) * mm, "end": v(31.75, -60.32) * mm, "construction": true});
            skLineSegment(sketch, "E238", {"start": v(-196.85, -127.63) * mm, "end": v(31.75, -127.63) * mm, "construction": true});
            skLineSegment(sketch, "E239.MirrorCS", {"start": v(-196.85, -56.51) * mm, "end": v(31.75, -56.51) * mm, "construction": true});
            skLineSegment(sketch, "E240", {"start": v(-177.16, -139.7) * mm, "end": v(-177.16, -44.45) * mm, "construction": true});
            skLineSegment(sketch, "E241", {"start": v(-133.35, -139.7) * mm, "end": v(-133.35, -44.45) * mm, "construction": true});
            skLineSegment(sketch, "E242", {"start": v(-12.7, -139.7) * mm, "end": v(-12.7, -44.45) * mm, "construction": true});
            skLineSegment(sketch, "E243", {"start": v(-196.85, -120.79) * mm, "end": v(-196.85, -63.36) * mm});
            skLineSegment(sketch, "E244", {"start": v(-194.49, -58.42) * mm, "end": v(-178.9, -45.86) * mm});
            skLineSegment(sketch, "E245", {"start": v(-174.92, -44.45) * mm, "end": v(-133.35, -44.45) * mm});
            skLineSegment(sketch, "E246", {"start": v(-133.35, -44.45) * mm, "end": v(-12.7, -56.51) * mm});
            skLineSegment(sketch, "E247", {"start": v(-12.7, -56.51) * mm, "end": v(25.4, -56.51) * mm});
            skLineSegment(sketch, "E248", {"start": v(31.75, -62.86) * mm, "end": v(31.75, -121.28) * mm});
            skLineSegment(sketch, "E249", {"start": v(25.4, -127.63) * mm, "end": v(-12.7, -127.63) * mm});
            skLineSegment(sketch, "E250", {"start": v(-12.7, -127.63) * mm, "end": v(-133.35, -139.7) * mm});
            skLineSegment(sketch, "E251", {"start": v(-133.35, -139.7) * mm, "end": v(-174.92, -139.7) * mm});
            skLineSegment(sketch, "E252", {"start": v(-178.9, -138.3) * mm, "end": v(-194.49, -125.73) * mm});
            skPoint(sketch, "E253.visualSharp", {"position": v(31.75, -127.63) * mm});
            skArc(sketch, "E253.filletArc", {"start": v(25.4, -127.63) * mm, "mid": v(29.9, -125.78) * mm, "end": v(31.75, -121.28) * mm});
            skPoint(sketch, "E254.visualSharp", {"position": v(31.75, -56.51) * mm});
            skArc(sketch, "E254.filletArc", {"start": v(31.75, -62.86) * mm, "mid": v(29.9, -58.37) * mm, "end": v(25.4, -56.51) * mm});
            skPoint(sketch, "E255.visualSharp", {"position": v(-196.85, -123.82) * mm});
            skArc(sketch, "E255.filletArc", {"start": v(-196.85, -120.79) * mm, "mid": v(-196.23, -123.53) * mm, "end": v(-194.49, -125.73) * mm});
            skPoint(sketch, "E256.visualSharp", {"position": v(-177.16, -139.7) * mm});
            skArc(sketch, "E256.filletArc", {"start": v(-178.9, -138.3) * mm, "mid": v(-177.04, -139.34) * mm, "end": v(-174.92, -139.7) * mm});
            skPoint(sketch, "E257.visualSharp", {"position": v(-196.85, -60.32) * mm});
            skArc(sketch, "E257.filletArc", {"start": v(-194.49, -58.42) * mm, "mid": v(-196.23, -60.62) * mm, "end": v(-196.85, -63.36) * mm});
            skPoint(sketch, "E258.visualSharp", {"position": v(-177.16, -44.45) * mm});
            skArc(sketch, "E258.filletArc", {"start": v(-174.92, -44.45) * mm, "mid": v(-177.04, -44.81) * mm, "end": v(-178.9, -45.86) * mm});
            skLineSegment(sketch, "E259", {"start": v(173.74, -116.84) * mm, "end": v(196.85, -116.84) * mm, "construction": true});
            skLineSegment(sketch, "E260.MirrorCS", {"start": v(160.32, -0.82) * mm, "end": v(137.54, 43.88) * mm});
            skLineSegment(sketch, "E261.MirrorCS", {"start": v(133.02, 41.57) * mm, "end": v(137.54, 43.88) * mm});
            skLineSegment(sketch, "E262", {"start": v(198.12, 122.87) * mm, "end": v(198.76, 122.87) * mm});
            skLineSegment(sketch, "E263", {"start": v(200.03, 121.6) * mm, "end": v(200.03, 114.62) * mm});
            skLineSegment(sketch, "E264", {"start": v(198.76, 113.35) * mm, "end": v(198.12, 113.35) * mm});
            skPoint(sketch, "E265.visualSharp", {"position": v(166.37, 82.55) * mm});
            skArc(sketch, "E265.filletArc", {"start": v(167.64, 82.55) * mm, "mid": v(166.74, 82.18) * mm, "end": v(166.37, 81.28) * mm});
            skPoint(sketch, "E266.visualSharp", {"position": v(147.32, 82.55) * mm});
            skArc(sketch, "E266.filletArc", {"start": v(147.32, 81.28) * mm, "mid": v(146.95, 82.18) * mm, "end": v(146.05, 82.55) * mm});
            skPoint(sketch, "E267.visualSharp", {"position": v(200.03, 113.35) * mm});
            skArc(sketch, "E267.filletArc", {"start": v(198.76, 113.35) * mm, "mid": v(199.65, 113.72) * mm, "end": v(200.03, 114.62) * mm});
            skPoint(sketch, "E268.visualSharp", {"position": v(200.03, 122.87) * mm});
            skArc(sketch, "E268.filletArc", {"start": v(200.03, 121.6) * mm, "mid": v(199.65, 122.5) * mm, "end": v(198.76, 122.87) * mm});
            skPoint(sketch, "E269.visualSharp", {"position": v(196.85, 122.87) * mm});
            skArc(sketch, "E269.filletArc", {"start": v(196.85, 124.13) * mm, "mid": v(197.23, 123.24) * mm, "end": v(198.12, 122.87) * mm});
            skPoint(sketch, "E270.visualSharp", {"position": v(196.85, 113.35) * mm});
            skArc(sketch, "E270.filletArc", {"start": v(198.12, 113.35) * mm, "mid": v(197.22, 112.98) * mm, "end": v(196.85, 112.08) * mm});
            skLineSegment(sketch, "E271", {"start": v(-196.85, 54.61) * mm, "end": v(31.75, 54.61) * mm, "construction": true});
            skLineSegment(sketch, "E272", {"start": v(-82.55, -27.94) * mm, "end": v(-82.55, 137.16) * mm, "construction": true});
            skLineSegment(sketch, "E273", {"start": v(0, 156.21) * mm, "end": v(0, -156.2) * mm, "construction": true});
            skLineSegment(sketch, "E274", {"start": v(-222.25, 0) * mm, "end": v(222.25, 0) * mm, "construction": true});
            skPoint(sketch, "E275", {"position": v(0, 0) * mm});
            skPoint(sketch, "E276", {"position": v(-82.55, 54.61) * mm});
            skPoint(sketch, "E277", {"position": v(-133.35, -92.07) * mm});
            skLineSegment(sketch, "E278", {"start": v(63.5, 106.68) * mm, "end": v(196.85, 106.68) * mm, "construction": true});
            skLineSegment(sketch, "E279", {"start": v(130.18, 130.81) * mm, "end": v(130.18, 82.55) * mm, "construction": true});
            skPoint(sketch, "E280", {"position": v(130.18, 106.68) * mm});
            skLineSegment(sketch, "E281", {"start": v(172.42, -24.58) * mm, "end": v(160.32, -0.82) * mm, "construction": true});
            skPoint(sketch, "E282", {"position": v(166.37, -12.7) * mm});
            skLineSegment(sketch, "E283", {"start": v(196.85, 124.46) * mm, "end": v(196.85, 124.13) * mm});
            skLineSegment(sketch, "E284", {"start": v(196.85, 124.13) * mm, "end": v(196.85, 112.08) * mm, "construction": true});
            skArc(sketch, "E285", {"start": v(31.75, -21.59) * mm, "mid": v(29.9, -26.08) * mm, "end": v(25.4, -27.94) * mm, "construction": true});
            skLineSegment(sketch, "E286.bottom", {"start": v(107.95, -137.16) * mm, "end": v(57.15, -137.16) * mm});
            skLineSegment(sketch, "E286.top", {"start": v(107.95, 66.04) * mm, "end": v(57.15, 66.04) * mm});
            skLineSegment(sketch, "E286.left", {"start": v(114.3, -130.8) * mm, "end": v(114.3, 59.69) * mm});
            skLineSegment(sketch, "E286.right", {"start": v(50.8, -130.8) * mm, "end": v(50.8, 59.69) * mm});
            skLineSegment(sketch, "E287", {"start": v(82.55, -137.16) * mm, "end": v(82.55, 66.04) * mm, "construction": true});
            skLineSegment(sketch, "E288", {"start": v(114.3, -35.56) * mm, "end": v(50.8, -35.56) * mm, "construction": true});
            skPoint(sketch, "E289", {"position": v(82.55, -35.56) * mm});
            skPoint(sketch, "E290.visualSharp", {"position": v(114.3, -137.16) * mm});
            skArc(sketch, "E290.filletArc", {"start": v(107.95, -137.16) * mm, "mid": v(112.44, -135.3) * mm, "end": v(114.3, -130.8) * mm});
            skPoint(sketch, "E291.visualSharp", {"position": v(50.8, -137.16) * mm});
            skArc(sketch, "E291.filletArc", {"start": v(50.8, -130.8) * mm, "mid": v(52.66, -135.3) * mm, "end": v(57.15, -137.16) * mm});
            skPoint(sketch, "E292.visualSharp", {"position": v(50.8, 66.04) * mm});
            skArc(sketch, "E292.filletArc", {"start": v(57.15, 66.04) * mm, "mid": v(52.66, 64.18) * mm, "end": v(50.8, 59.69) * mm});
            skPoint(sketch, "E293.visualSharp", {"position": v(114.3, 66.04) * mm});
            skArc(sketch, "E293.filletArc", {"start": v(114.3, 59.69) * mm, "mid": v(112.44, 64.18) * mm, "end": v(107.95, 66.04) * mm});
            skLineSegment(sketch, "E294", {"start": v(185.3, -91.44) * mm, "end": v(185.3, -128.4) * mm, "construction": true});
            skLineSegment(sketch, "E295.bottom", {"start": v(-193.68, 143.5) * mm, "end": v(28.58, 143.5) * mm});
            skLineSegment(sketch, "E295.top", {"start": v(-193.68, -34.3) * mm, "end": v(0, -34.3) * mm});
            skLineSegment(sketch, "E295.left", {"start": v(-206.38, 130.8) * mm, "end": v(-206.38, 111.76) * mm});
            skLineSegment(sketch, "E295.right", {"start": v(41.28, 130.8) * mm, "end": v(41.27, -21.6) * mm});
            skPoint(sketch, "E296.visualSharp", {"position": v(-206.38, 143.5) * mm});
            skArc(sketch, "E296.filletArc", {"start": v(-193.68, 143.5) * mm, "mid": v(-202.66, 139.8) * mm, "end": v(-206.38, 130.8) * mm});
            skPoint(sketch, "E297.visualSharp", {"position": v(41.28, 143.5) * mm});
            skArc(sketch, "E297.filletArc", {"start": v(41.28, 130.8) * mm, "mid": v(37.56, 139.8) * mm, "end": v(28.58, 143.51) * mm});
            skPoint(sketch, "E298.visualSharp", {"position": v(41.27, -34.3) * mm});
            skArc(sketch, "E298.filletArc", {"start": v(28.57, -34.3) * mm, "mid": v(37.56, -30.57) * mm, "end": v(41.27, -21.6) * mm});
            skPoint(sketch, "E299.visualSharp", {"position": v(-206.38, -34.3) * mm});
            skArc(sketch, "E299.filletArc", {"start": v(-206.38, -21.6) * mm, "mid": v(-202.66, -30.57) * mm, "end": v(-193.68, -34.3) * mm});
            skArc(sketch, "E300", {"start": v(-206.38, 62.23) * mm, "mid": v(-214, 54.6) * mm, "end": v(-206.38, 46.99) * mm});
            skLineSegment(sketch, "E301", {"start": v(-206.38, 62.23) * mm, "end": v(-206.38, 46.99) * mm, "construction": true});
            skLineSegment(sketch, "E302", {"start": v(-206.38, 46.99) * mm, "end": v(-206.38, -21.6) * mm});
            skArc(sketch, "E303", {"start": v(124.46, -93.98) * mm, "mid": v(139.7, -78.74) * mm, "end": v(154.94, -93.98) * mm});
            skArc(sketch, "E304", {"start": v(154.94, -124.46) * mm, "mid": v(139.7, -139.7) * mm, "end": v(124.46, -124.46) * mm});
            skArc(sketch, "E305", {"start": v(173.74, -91.44) * mm, "mid": v(185.3, -79.88) * mm, "end": v(196.85, -91.44) * mm});
            skLineSegment(sketch, "E306", {"start": v(-193.68, 111.76) * mm, "end": v(0, 111.76) * mm});
            skLineSegment(sketch, "E307", {"start": v(12.7, 99.06) * mm, "end": v(12.7, -21.6) * mm});
            skPoint(sketch, "E308.visualSharp", {"position": v(12.7, 111.76) * mm});
            skArc(sketch, "E308.filletArc", {"start": v(12.7, 99.06) * mm, "mid": v(8.98, 108.04) * mm, "end": v(0, 111.76) * mm});
            skLineSegment(sketch, "E309", {"start": v(-206.38, 99.06) * mm, "end": v(-206.38, 62.23) * mm});
            skLineSegment(sketch, "E310", {"start": v(12.7, -34.3) * mm, "end": v(28.57, -34.3) * mm});
            skPoint(sketch, "E311.visualSharp", {"position": v(-206.38, 111.76) * mm});
            skArc(sketch, "E311.filletArc", {"start": v(-193.68, 111.76) * mm, "mid": v(-202.66, 108.04) * mm, "end": v(-206.38, 99.06) * mm});
            skPoint(sketch, "E312.visualSharp", {"position": v(12.7, -34.29) * mm});
            skArc(sketch, "E312.filletArc", {"start": v(0, -34.3) * mm, "mid": v(8.98, -30.57) * mm, "end": v(12.7, -21.6) * mm});
            skLineSegment(sketch, "E313", {"start": v(-206.38, 111.76) * mm, "end": v(-206.38, 99.06) * mm});
            skLineSegment(sketch, "E314", {"start": v(12.7, -34.3) * mm, "end": v(0, -34.3) * mm});
            skLineSegment(sketch, "E315", {"start": v(173.74, -106.68) * mm, "end": v(196.85, -106.68) * mm});
            skSolve(sketch);
        }
        {
            var Q0;
            Q0 = qSketchRegion(id + "F4", true);
            extrude(context, id + "F5", {"entities" : qUnion([Q0]), "depth" : 12.7 * mm, "offsetDistance" : 25.4 * mm});
        }
    });
